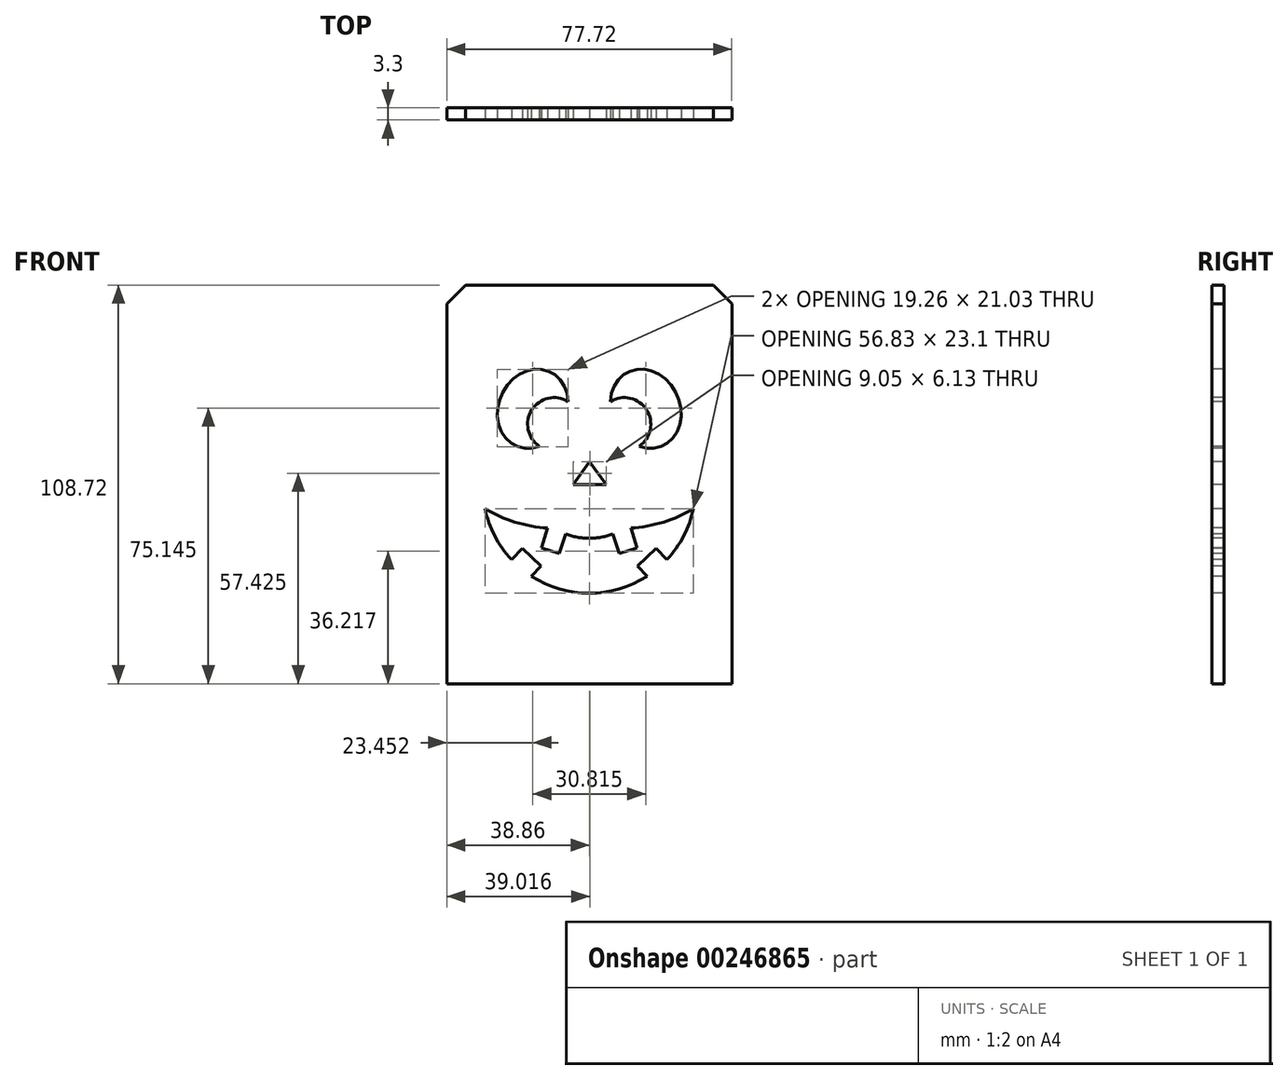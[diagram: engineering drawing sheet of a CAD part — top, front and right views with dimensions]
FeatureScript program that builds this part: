
annotation { "Feature Type Name" : "Feature", "Feature Type Description" : "" }
export const myFeature = defineFeature(function(context is Context, id is Id, definition is map)
    precondition{}
    {
        {
            var Q0;
            Q0=qCreatedBy(makeId("Front.planeOp"),FACE);
            var sketch = newSketch(context, id + "F0", { "sketchPlane" : qUnion([Q0])});
            skLineSegment(sketch, "E0.bottom", {"start": v(38.86, 54.36) * mm, "end": v(-38.86, 54.36) * mm});
            skLineSegment(sketch, "E0.top", {"start": v(38.86, -54.36) * mm, "end": v(-38.86, -54.36) * mm});
            skLineSegment(sketch, "E0.left", {"start": v(38.86, 54.36) * mm, "end": v(38.86, -54.36) * mm});
            skLineSegment(sketch, "E0.right", {"start": v(-38.86, 54.36) * mm, "end": v(-38.86, -54.36) * mm});
            skPoint(sketch, "E0.middle", {"position": v(0, 0) * mm});
            skSolve(sketch);
        }
        {
            var Q0;
            Q0=qSketchRegion(id+"F0",true);
            extrude(context, id + "F1", {"entities" : qUnion([Q0]), "depth" : 3.3 * mm});
        }
        {
            var Q0;
            Q0=makeQuery(id+"F1.opExtrude","CAP_FACE",FACE,{"disambiguationData":[OSD([sQuery(id+"F0.wireOp",EDGE,"E0.bottom"),sQuery(id+"F0.wireOp",EDGE,"E0.top"),sQuery(id+"F0.wireOp",EDGE,"E0.left"),sQuery(id+"F0.wireOp",EDGE,"E0.right")])],"isStart":false});
            var sketch = newSketch(context, id + "F2", { "sketchPlane" : qUnion([Q0])});
            skLineSegment(sketch, "E1", {"start": v(0, 57.24) * mm, "end": v(0, -57.24) * mm, "construction": true});
            skLineSegment(sketch, "E2", {"start": v(-50.8, 0) * mm, "end": v(50.8, 0) * mm, "construction": true});
            skArc(sketch, "E3", {"start": v(35.44, -3.57) * mm, "mid": v(31.46, -11.87) * mm, "end": v(32.26, -21.03) * mm});
            skLineSegment(sketch, "E4", {"start": v(15.88, -44.54) * mm, "end": v(0, -44.54) * mm, "construction": true});
            skArc(sketch, "E5", {"start": v(15.88, -44.54) * mm, "mid": v(30.2, -37.06) * mm, "end": v(32.26, -21.03) * mm});
            skArc(sketch, "E6", {"start": v(15.88, -44.54) * mm, "mid": v(7.78, -45.34) * mm, "end": v(0, -47.71) * mm});
            skArc(sketch, "E7.MirrorCS", {"start": v(-15.87, -44.54) * mm, "mid": v(-7.78, -45.34) * mm, "end": v(0, -47.71) * mm});
            skArc(sketch, "E8.MirrorCS", {"start": v(-15.87, -44.54) * mm, "mid": v(-30.2, -37.06) * mm, "end": v(-32.26, -21.03) * mm});
            skArc(sketch, "E9.MirrorCS", {"start": v(-35.44, -3.57) * mm, "mid": v(-31.46, -11.87) * mm, "end": v(-32.26, -21.03) * mm});
            skArc(sketch, "E10.MirrorCS", {"start": v(-35.44, 3.57) * mm, "mid": v(-31.46, 11.87) * mm, "end": v(-32.26, 21.03) * mm});
            skArc(sketch, "E11.MirrorCS", {"start": v(-15.88, 44.54) * mm, "mid": v(-30.2, 37.06) * mm, "end": v(-32.26, 21.03) * mm});
            skArc(sketch, "E12.MirrorCS", {"start": v(-15.88, 44.54) * mm, "mid": v(-7.78, 45.34) * mm, "end": v(0, 47.71) * mm});
            skArc(sketch, "E13.MirrorCS", {"start": v(15.87, 44.54) * mm, "mid": v(7.78, 45.34) * mm, "end": v(0, 47.71) * mm});
            skArc(sketch, "E14.MirrorCS", {"start": v(15.87, 44.54) * mm, "mid": v(30.2, 37.06) * mm, "end": v(32.26, 21.03) * mm});
            skArc(sketch, "E15.MirrorCS", {"start": v(35.44, 3.57) * mm, "mid": v(31.46, 11.87) * mm, "end": v(32.26, 21.03) * mm});
            skArc(sketch, "E16", {"start": v(35.44, 3.57) * mm, "mid": v(34.41, 0) * mm, "end": v(35.44, -3.57) * mm});
            skPoint(sketch, "E17.orphan", {"position": v(39.69, 0) * mm});
            skArc(sketch, "E18.MirrorCS", {"start": v(-35.44, 3.57) * mm, "mid": v(-34.41, 0) * mm, "end": v(-35.44, -3.57) * mm});
            skPoint(sketch, "E19.orphan", {"position": v(-39.69, 0) * mm});
            skSolve(sketch);
        }
        {
            var Q0;
            Q0=makeQuery(id+"F2.imprint","IMPRINT",FACE,{"disambiguationData":[TD([[makeQuery(id+"F2.imprint","IMPRINT",EDGE,{"derivedFrom":sQuery(id+"F2.wireOp",EDGE,"E3")}),1.0]])]});
            var sketch = newSketch(context, id + "F3", { "sketchPlane" : qUnion([Q0])});
            skFitSpline(sketch, "E20", {"points": [v(-34.74, -25) * mm, v(-17.68, -23.14) * mm, v(0, -25.84) * mm, v(18.3, -28) * mm, v(33.6, -24.4) * mm], "startDerivative": vector(68.08, 28.42) * mm, "endDerivative": vector(41.75, 55.86) * mm});
            skArc(sketch, "E21.0", {"start": v(15.88, -44.54) * mm, "mid": v(28.97, -38.63) * mm, "end": v(33.2, -24.9) * mm});
            skArc(sketch, "E22.0", {"start": v(-15.87, -44.54) * mm, "mid": v(-29.14, -38.43) * mm, "end": v(-33.13, -24.38) * mm});
            skArc(sketch, "E23.0", {"start": v(15.88, -44.54) * mm, "mid": v(7.78, -45.34) * mm, "end": v(0, -47.71) * mm});
            skArc(sketch, "E23.1", {"start": v(-15.87, -44.54) * mm, "mid": v(-7.78, -45.34) * mm, "end": v(0, -47.71) * mm});
            skPoint(sketch, "E24.orphan", {"position": v(-32.26, -21.03) * mm});
            skLineSegment(sketch, "E25.bottom", {"start": v(23.58, -32.65) * mm, "end": v(5.44, -32.65) * mm, "construction": true});
            skLineSegment(sketch, "E25.top", {"start": v(23.58, -12.55) * mm, "end": v(5.44, -12.55) * mm, "construction": true});
            skLineSegment(sketch, "E25.left", {"start": v(23.58, -32.65) * mm, "end": v(23.58, -12.55) * mm, "construction": true});
            skLineSegment(sketch, "E25.right", {"start": v(5.44, -32.65) * mm, "end": v(5.44, -12.55) * mm, "construction": true});
            skArc(sketch, "E26", {"start": v(6.5, -26.77) * mm, "mid": v(6.6, -19.6) * mm, "end": v(5.44, -12.55) * mm});
            skArc(sketch, "E27", {"start": v(23.58, -12.55) * mm, "mid": v(22.47, -20.37) * mm, "end": v(22.78, -28.26) * mm});
            skLineSegment(sketch, "E28", {"start": v(0.57, -13.45) * mm, "end": v(5.44, -12.55) * mm});
            skLineSegment(sketch, "E29", {"start": v(28.46, 0) * mm, "end": v(0.57, 0) * mm, "construction": true});
            skArc(sketch, "E30", {"start": v(-2.4, -8.48) * mm, "mid": v(-2.65, -12) * mm, "end": v(0.57, -13.45) * mm});
            skArc(sketch, "E31", {"start": v(0, -10.42) * mm, "mid": v(-0.23, -8.24) * mm, "end": v(-2.4, -8.48) * mm});
            skArc(sketch, "E32", {"start": v(0, -10.42) * mm, "mid": v(-0.04, -11.92) * mm, "end": v(1.4, -12.35) * mm});
            skArc(sketch, "E33", {"start": v(1.4, -12.35) * mm, "mid": v(5.55, -5.86) * mm, "end": v(0.57, 0) * mm});
            skLineSegment(sketch, "E34", {"start": v(14.51, 0) * mm, "end": v(14.51, -12.55) * mm, "construction": true});
            skArc(sketch, "E35.MirrorCS", {"start": v(27.61, -12.35) * mm, "mid": v(23.47, -5.86) * mm, "end": v(28.46, 0) * mm});
            skLineSegment(sketch, "E36.MirrorCS", {"start": v(28.46, -13.45) * mm, "end": v(23.58, -12.55) * mm});
            skArc(sketch, "E37.MirrorCS", {"start": v(31.42, -8.48) * mm, "mid": v(31.67, -12) * mm, "end": v(28.46, -13.45) * mm});
            skArc(sketch, "E38.MirrorCS", {"start": v(29.02, -10.42) * mm, "mid": v(29.25, -8.24) * mm, "end": v(31.42, -8.48) * mm});
            skArc(sketch, "E39.MirrorCS", {"start": v(29.02, -10.42) * mm, "mid": v(29.06, -11.92) * mm, "end": v(27.61, -12.35) * mm});
            skArc(sketch, "E40", {"start": v(0.57, 0) * mm, "mid": v(5.65, -0.6) * mm, "end": v(10.76, -0.93) * mm});
            skLineSegment(sketch, "E41", {"start": v(10.76, -0.93) * mm, "end": v(8.47, 9.06) * mm});
            skLineSegment(sketch, "E42", {"start": v(8.47, 9.06) * mm, "end": v(6.8, 8.68) * mm});
            skArc(sketch, "E43", {"start": v(7.7, 9.94) * mm, "mid": v(5.6, 10.49) * mm, "end": v(6.8, 8.68) * mm});
            skLineSegment(sketch, "E44", {"start": v(14.51, 0) * mm, "end": v(14.77, 8.31) * mm, "construction": true});
            skLineSegment(sketch, "E45.MirrorCS", {"start": v(18.26, -0.93) * mm, "end": v(21.1, 8.66) * mm});
            skLineSegment(sketch, "E46.MirrorCS", {"start": v(21.1, 8.66) * mm, "end": v(22.75, 8.18) * mm});
            skArc(sketch, "E47.MirrorCS", {"start": v(21.93, 9.5) * mm, "mid": v(24.07, 9.9) * mm, "end": v(22.75, 8.18) * mm});
            skArc(sketch, "E48", {"start": v(7.7, 9.94) * mm, "mid": v(12.62, 15.22) * mm, "end": v(14.1, 22.28) * mm});
            skArc(sketch, "E49", {"start": v(15.59, 22.28) * mm, "mid": v(17.1, 15.06) * mm, "end": v(21.93, 9.5) * mm});
            skLineSegment(sketch, "E50", {"start": v(14.1, 22.28) * mm, "end": v(12.75, 29.94) * mm});
            skLineSegment(sketch, "E51", {"start": v(12.75, 29.94) * mm, "end": v(10.25, 29.5) * mm});
            skLineSegment(sketch, "E52", {"start": v(10.25, 29.5) * mm, "end": v(10.04, 30.72) * mm});
            skLineSegment(sketch, "E53", {"start": v(10.04, 30.72) * mm, "end": v(12.66, 31.3) * mm});
            skLineSegment(sketch, "E54", {"start": v(12.66, 31.3) * mm, "end": v(12.12, 34.79) * mm});
            skLineSegment(sketch, "E55", {"start": v(12.12, 34.79) * mm, "end": v(14.24, 35.11) * mm});
            skLineSegment(sketch, "E56", {"start": v(14.24, 35.11) * mm, "end": v(14.8, 31.45) * mm});
            skLineSegment(sketch, "E57", {"start": v(14.8, 31.45) * mm, "end": v(17.72, 31.9) * mm});
            skLineSegment(sketch, "E58", {"start": v(17.72, 31.9) * mm, "end": v(17.99, 30.17) * mm});
            skLineSegment(sketch, "E59", {"start": v(17.99, 30.17) * mm, "end": v(14.89, 29.68) * mm});
            skLineSegment(sketch, "E60", {"start": v(14.89, 29.68) * mm, "end": v(15.59, 22.28) * mm});
            skArc(sketch, "E61.trimOffspring", {"start": v(18.26, -0.93) * mm, "mid": v(23.37, -0.6) * mm, "end": v(28.46, 0) * mm});
            skPoint(sketch, "E62.orphan", {"position": v(18.2, -1.17) * mm});
            skLineSegment(sketch, "E63", {"start": v(8.48, -4.98) * mm, "end": v(9.12, -7.41) * mm});
            skLineSegment(sketch, "E64", {"start": v(9.77, -9.85) * mm, "end": v(10.94, -9.54) * mm});
            skLineSegment(sketch, "E65", {"start": v(12.72, -9.06) * mm, "end": v(12.26, -7.34) * mm});
            skLineSegment(sketch, "E66", {"start": v(11.56, -4.7) * mm, "end": v(10.33, -4.82) * mm});
            skLineSegment(sketch, "E67", {"start": v(9.75, -4.87) * mm, "end": v(10.34, -7.13) * mm});
            skLineSegment(sketch, "E68", {"start": v(10.34, -7.13) * mm, "end": v(9.12, -7.41) * mm});
            skLineSegment(sketch, "E69", {"start": v(10.33, -4.82) * mm, "end": v(10.9, -7.06) * mm});
            skLineSegment(sketch, "E70", {"start": v(10.9, -7.06) * mm, "end": v(12.14, -6.89) * mm});
            skLineSegment(sketch, "E71", {"start": v(9.29, -8.05) * mm, "end": v(10.46, -7.73) * mm});
            skLineSegment(sketch, "E72", {"start": v(10.46, -7.73) * mm, "end": v(10.94, -9.54) * mm});
            skLineSegment(sketch, "E73", {"start": v(11.57, -9.37) * mm, "end": v(11.12, -7.64) * mm});
            skLineSegment(sketch, "E74", {"start": v(11.12, -7.64) * mm, "end": v(12.26, -7.34) * mm});
            skLineSegment(sketch, "E75.trimOffspring", {"start": v(12.14, -6.89) * mm, "end": v(11.56, -4.7) * mm});
            skLineSegment(sketch, "E76.trimOffspring", {"start": v(9.75, -4.87) * mm, "end": v(8.48, -4.98) * mm});
            skLineSegment(sketch, "E77.trimOffspring", {"start": v(9.29, -8.05) * mm, "end": v(9.77, -9.85) * mm});
            skLineSegment(sketch, "E78.trimOffspring", {"start": v(11.57, -9.37) * mm, "end": v(12.72, -9.06) * mm});
            skLineSegment(sketch, "E79.MirrorCS", {"start": v(17.46, -4.7) * mm, "end": v(18.69, -4.82) * mm});
            skLineSegment(sketch, "E80.MirrorCS", {"start": v(19.27, -4.87) * mm, "end": v(18.68, -7.13) * mm});
            skLineSegment(sketch, "E81.MirrorCS", {"start": v(17.45, -9.37) * mm, "end": v(17.9, -7.64) * mm});
            skLineSegment(sketch, "E82.MirrorCS", {"start": v(18.68, -7.13) * mm, "end": v(19.9, -7.41) * mm});
            skLineSegment(sketch, "E83.MirrorCS", {"start": v(17.9, -7.64) * mm, "end": v(16.76, -7.34) * mm});
            skLineSegment(sketch, "E84.MirrorCS", {"start": v(18.69, -4.82) * mm, "end": v(18.12, -7.06) * mm});
            skLineSegment(sketch, "E85.MirrorCS", {"start": v(16.88, -6.89) * mm, "end": v(17.46, -4.7) * mm});
            skLineSegment(sketch, "E86.MirrorCS", {"start": v(18.12, -7.06) * mm, "end": v(16.88, -6.89) * mm});
            skLineSegment(sketch, "E87.MirrorCS", {"start": v(19.27, -4.87) * mm, "end": v(20.54, -4.98) * mm});
            skLineSegment(sketch, "E88.MirrorCS", {"start": v(20.54, -4.98) * mm, "end": v(19.9, -7.41) * mm});
            skLineSegment(sketch, "E89.MirrorCS", {"start": v(19.73, -8.05) * mm, "end": v(18.56, -7.73) * mm});
            skLineSegment(sketch, "E90.MirrorCS", {"start": v(19.73, -8.05) * mm, "end": v(19.25, -9.85) * mm});
            skLineSegment(sketch, "E91.MirrorCS", {"start": v(19.25, -9.85) * mm, "end": v(18.08, -9.54) * mm});
            skLineSegment(sketch, "E92.MirrorCS", {"start": v(18.56, -7.73) * mm, "end": v(18.08, -9.54) * mm});
            skLineSegment(sketch, "E93.MirrorCS", {"start": v(17.45, -9.37) * mm, "end": v(16.3, -9.06) * mm});
            skLineSegment(sketch, "E94.MirrorCS", {"start": v(16.3, -9.06) * mm, "end": v(16.76, -7.34) * mm});
            skArc(sketch, "E95", {"start": v(14.28, 11.97) * mm, "mid": v(12.23, 10.98) * mm, "end": v(11.15, 8.98) * mm});
            skLineSegment(sketch, "E96", {"start": v(14.28, 11.97) * mm, "end": v(14.28, 8.98) * mm});
            skLineSegment(sketch, "E97", {"start": v(15.17, 4.65) * mm, "end": v(15.17, 7.88) * mm});
            skLineSegment(sketch, "E98", {"start": v(18.4, 8.98) * mm, "end": v(15.17, 8.98) * mm});
            skLineSegment(sketch, "E99", {"start": v(11.1, 7.88) * mm, "end": v(14.28, 7.88) * mm});
            skLineSegment(sketch, "E100.trimOffspring", {"start": v(15.17, 8.98) * mm, "end": v(15.17, 11.98) * mm});
            skLineSegment(sketch, "E101.trimOffspring", {"start": v(15.17, 7.88) * mm, "end": v(18.43, 7.88) * mm});
            skLineSegment(sketch, "E102.trimOffspring", {"start": v(14.28, 7.88) * mm, "end": v(14.28, 4.66) * mm});
            skLineSegment(sketch, "E103.trimOffspring", {"start": v(14.28, 8.98) * mm, "end": v(11.15, 8.98) * mm});
            skArc(sketch, "E104.trimOffspring", {"start": v(11.1, 7.88) * mm, "mid": v(12.14, 5.73) * mm, "end": v(14.28, 4.66) * mm});
            skArc(sketch, "E105.trimOffspring", {"start": v(18.4, 8.98) * mm, "mid": v(17.28, 11.01) * mm, "end": v(15.17, 11.98) * mm});
            skArc(sketch, "E106.trimOffspring", {"start": v(15.17, 4.65) * mm, "mid": v(17.37, 5.7) * mm, "end": v(18.43, 7.88) * mm});
            skLineSegment(sketch, "E107.left", {"start": v(12.04, -27.4) * mm, "end": v(12.04, -21.48) * mm});
            skLineSegment(sketch, "E107.right", {"start": v(16, -27.8) * mm, "end": v(16, -21.48) * mm});
            skArc(sketch, "E108", {"start": v(16, -21.48) * mm, "mid": v(14.02, -19.5) * mm, "end": v(12.04, -21.48) * mm});
            skLineSegment(sketch, "E109", {"start": v(12.04, -27.4) * mm, "end": v(16, -27.8) * mm});
            skArc(sketch, "E110.0", {"start": v(-35.44, -3.57) * mm, "mid": v(-31.46, -11.87) * mm, "end": v(-32.26, -21.03) * mm, "construction": true});
            skArc(sketch, "E110.1", {"start": v(15.87, 44.54) * mm, "mid": v(7.78, 45.34) * mm, "end": v(0, 47.71) * mm});
            skArc(sketch, "E110.2", {"start": v(-15.88, 44.54) * mm, "mid": v(-30.2, 37.06) * mm, "end": v(-32.26, 21.03) * mm, "construction": true});
            skArc(sketch, "E110.3", {"start": v(-35.44, 3.57) * mm, "mid": v(-34.41, 0) * mm, "end": v(-35.44, -3.57) * mm, "construction": true});
            skArc(sketch, "E110.4", {"start": v(-35.44, 3.57) * mm, "mid": v(-31.46, 11.87) * mm, "end": v(-32.26, 21.03) * mm});
            skArc(sketch, "E110.5", {"start": v(-15.88, 44.54) * mm, "mid": v(-7.78, 45.34) * mm, "end": v(0, 47.71) * mm});
            skArc(sketch, "E111", {"start": v(-17.1, 9.66) * mm, "mid": v(-3.37, 14.89) * mm, "end": v(1.5, 28.74) * mm});
            skArc(sketch, "E112", {"start": v(-17.1, 9.66) * mm, "mid": v(-26.87, 8.42) * mm, "end": v(-35.44, 3.57) * mm});
            skArc(sketch, "E113", {"start": v(15.87, 44.54) * mm, "mid": v(5.2, 39.82) * mm, "end": v(1.5, 28.74) * mm});
            skArc(sketch, "E114.trimOffspring", {"start": v(-15.88, 44.54) * mm, "mid": v(-30.2, 37.06) * mm, "end": v(-32.26, 21.03) * mm});
            skArc(sketch, "E115", {"start": v(-24.92, -22.89) * mm, "mid": v(-23.55, -16.2) * mm, "end": v(-24.4, -9.44) * mm});
            skFitSpline(sketch, "E116", {"points": [v(-24.4, -9.44) * mm, v(-26.98, -10.38) * mm, v(-27.97, -8.39) * mm, v(-29.93, -8.52) * mm, v(-30.92, -6) * mm, v(-32.1, -5.52) * mm, v(-32.53, -4.18) * mm, v(-32.18, -3.27) * mm, v(-31.84, -4.44) * mm, v(-31.05, -4.83) * mm, v(-31.49, -2) * mm, v(-30.88, -2.14) * mm, v(-30.1, -5.05) * mm, v(-29.45, -3.57) * mm, v(-28.71, -3.66) * mm, v(-29.54, -5.78) * mm, v(-29.23, -7.17) * mm, v(-27.54, -7.04) * mm, v(-26.28, -8.52) * mm, v(-24.4, -7.6) * mm], "startDerivative": vector(-46.53, -30.94) * mm, "endDerivative": vector(36.03, 29.74) * mm});
            skArc(sketch, "E117", {"start": v(-24.4, -7.6) * mm, "mid": v(-24.93, -4.98) * mm, "end": v(-25.9, -2.49) * mm});
            skFitSpline(sketch, "E118", {"points": [v(-25.9, -2.49) * mm, v(-27.5, -1.49) * mm, v(-28.76, -1.49) * mm, v(-29.23, 0) * mm, v(-31.14, 0) * mm, v(-30.8, 3.42) * mm, v(-29.97, 3.55) * mm, v(-30.27, 1.77) * mm, v(-29.54, 1.72) * mm, v(-28.8, 4.59) * mm, v(-27.67, 4.37) * mm, v(-28.28, 1.98) * mm, v(-27.84, 0) * mm, v(-27.2, 2.46) * mm, v(-25.9, 2.37) * mm, v(-25.9, 0) * mm, v(-24.11, -2.49) * mm, v(-22.72, -5.26) * mm, v(-21.68, -4.18) * mm, v(-23.16, 1.33) * mm, v(-20.82, 1.46) * mm, v(-20.82, 3.02) * mm], "startDerivative": vector(-33.14, 31.82) * mm, "endDerivative": vector(-15.18, 49.9) * mm});
            skFitSpline(sketch, "E119", {"points": [v(-20.82, 3.02) * mm, v(-19.2, 3.92) * mm, v(-20.04, 5.84) * mm, v(-20.82, 8.3) * mm, v(-20.04, 8.38) * mm, v(-19.62, 6.46) * mm, v(-18.62, 5.34) * mm, v(-18.96, 7.3) * mm, v(-18.2, 7.55) * mm, v(-18.12, 4.13) * mm, v(-19.33, 2.25) * mm, v(-19.46, 0.87) * mm, v(-20.82, 0) * mm, v(-20.04, -3.35) * mm, v(-16.32, 0) * mm, v(-17.1, 1.46) * mm, v(-15.74, 3.02) * mm, v(-15.45, 5.84) * mm, v(-14.49, 5.55) * mm, v(-14.82, 3.02) * mm, v(-14.53, 1.46) * mm, v(-13.36, 4) * mm, v(-12.02, 3.02) * mm, v(-14.2, 0) * mm, v(-17.1, -4.06) * mm, v(-17.1, -7.4) * mm, v(-14.36, -5.44) * mm, v(-14.57, -4.1) * mm, v(-12.78, -3.22) * mm, v(-12.53, -1.68) * mm, v(-10.44, -0.8) * mm, v(-10.27, 1.46) * mm, v(-9.35, 0) * mm, v(-8.6, 3.02) * mm, v(-8.1, 0) * mm, v(-9.44, -1.26) * mm, v(-11.31, -3.26) * mm, v(-13.15, -4.6) * mm, v(-13.36, -6.6) * mm, v(-15.78, -8.94) * mm], "startDerivative": vector(94.65, 30.69) * mm, "endDerivative": vector(-102.82, -69.25) * mm});
            skArc(sketch, "E120", {"start": v(-15.78, -8.94) * mm, "mid": v(-16.8, -16.14) * mm, "end": v(-15.78, -23.34) * mm});
            skFitSpline(sketch, "E121", {"points": [v(-22.4, -11.55) * mm, v(-21.43, -13.07) * mm, v(-21.4, -14.11) * mm, v(-20.72, -14.36) * mm, v(-20.54, -13.59) * mm, v(-20.94, -12.02) * mm, v(-21.71, -11.06) * mm, v(-22.67, -10.07) * mm, v(-22.4, -11.55) * mm]});
            skFitSpline(sketch, "E122", {"points": [v(-18.38, -10.1) * mm, v(-19.09, -11.5) * mm, v(-19.21, -12.7) * mm, v(-19.15, -14.02) * mm, v(-18.84, -14.6) * mm, v(-18.38, -14.05) * mm, v(-18.26, -13.1) * mm, v(-18.56, -12.32) * mm, v(-18.29, -11.28) * mm, v(-17.6, -10.38) * mm, v(-18.38, -10.1) * mm]});
            skFitSpline(sketch, "E123", {"points": [v(-20.3, -15.78) * mm, v(-20.35, -17.1) * mm, v(-20.9, -18.47) * mm, v(-21.8, -19.67) * mm, v(-21.9, -21.46) * mm, v(-20.45, -21.43) * mm, v(-19.64, -20.38) * mm, v(-19.43, -18.84) * mm, v(-19.7, -17.85) * mm, v(-19.7, -16.37) * mm, v(-19.43, -15.38) * mm, v(-20.3, -15.78) * mm]});
            skCircle(sketch, "E124", {"center": v(-15.88, 27.08) * mm, "radius": 13.34 * mm});
            skSolve(sketch);
        }
        {
            var Q0;
            Q0=qSketchRegion(id+"F3",true);
            extrude(context, id + "F4", {"entities" : qUnion([Q0]), "operationType" : NewBodyOperationType.ADD, "oppositeDirection" : true, "depth" : 3.3 * mm});
        }
        {
            var Q0;
            Q0=makeQuery(id+"F1.opExtrude","SWEPT_EDGE",EDGE,{"disambiguationData":[OSD([sQuery(id+"F0.wireOp",EDGE,"E0.bottom"),sQuery(id+"F0.wireOp",EDGE,"E0.right")])]});
            var Q1;
            Q1=makeQuery(id+"F1.opExtrude","SWEPT_EDGE",EDGE,{"disambiguationData":[OSD([sQuery(id+"F0.wireOp",EDGE,"E0.bottom"),sQuery(id+"F0.wireOp",EDGE,"E0.left")])]});
            chamfer(context, id + "F5", {"entities" : qUnion([Q0, Q1]), "width" : 5.08 * mm, "tangentPropagation" : true});
        }
        {
            var Q0;
            Q0=makeQuery(id+"F2.imprint","IMPRINT",FACE,{"disambiguationData":[TD([[makeQuery(id+"F2.imprint","IMPRINT",EDGE,{"derivedFrom":sQuery(id+"F2.wireOp",EDGE,"E3")}),-1.0]])]});
            var sketch = newSketch(context, id + "F6", { "sketchPlane" : qUnion([Q0])});
            skEllipticalArc(sketch, "E125", {});
            skArc(sketch, "E126", {"start": v(13.61, 10.39) * mm, "mid": v(15.64, 20.31) * mm, "end": v(5.78, 22.6) * mm});
            skLineSegment(sketch, "E127", {"start": v(0, 6.13) * mm, "end": v(-4.37, 0) * mm});
            skLineSegment(sketch, "E128", {"start": v(-4.37, 0) * mm, "end": v(4.68, 0) * mm});
            skLineSegment(sketch, "E129", {"start": v(4.68, 0) * mm, "end": v(0, 6.13) * mm});
            skArc(sketch, "E130", {"start": v(0, -29.7) * mm, "mid": v(8.21, -28.5) * mm, "end": v(15.75, -25.05) * mm});
            skLineSegment(sketch, "E131", {"start": v(0, -29.7) * mm, "end": v(-13.21, -29.7) * mm, "construction": true});
            skLineSegment(sketch, "E132", {"start": v(15.75, -25.05) * mm, "end": v(13.12, -22.27) * mm});
            skLineSegment(sketch, "E133", {"start": v(13.12, -22.27) * mm, "end": v(18.25, -17.41) * mm});
            skLineSegment(sketch, "E134", {"start": v(18.25, -17.41) * mm, "end": v(21.18, -20.51) * mm});
            skArc(sketch, "E135", {"start": v(21.18, -20.51) * mm, "mid": v(25.76, -14.05) * mm, "end": v(28.42, -6.6) * mm});
            skArc(sketch, "E136", {"start": v(11.32, -11.88) * mm, "mid": v(20.2, -10.3) * mm, "end": v(28.42, -6.6) * mm});
            skLineSegment(sketch, "E137", {"start": v(11.32, -11.88) * mm, "end": v(13.01, -17.26) * mm});
            skLineSegment(sketch, "E138", {"start": v(13.01, -17.26) * mm, "end": v(8.13, -18.8) * mm});
            skLineSegment(sketch, "E139", {"start": v(8.13, -18.8) * mm, "end": v(6.47, -13.5) * mm});
            skArc(sketch, "E140", {"start": v(0, -14.68) * mm, "mid": v(3.3, -14.41) * mm, "end": v(6.47, -13.5) * mm});
            skEllipticalArc(sketch, "E141.MirrorCS", {});
            skArc(sketch, "E142.MirrorCS", {"start": v(-13.61, 10.39) * mm, "mid": v(-15.64, 20.31) * mm, "end": v(-5.78, 22.6) * mm});
            skArc(sketch, "E143.MirrorCS", {"start": v(-11.32, -11.88) * mm, "mid": v(-20.2, -10.3) * mm, "end": v(-28.42, -6.6) * mm});
            skArc(sketch, "E144.MirrorCS", {"start": v(-21.18, -20.51) * mm, "mid": v(-25.76, -14.05) * mm, "end": v(-28.42, -6.6) * mm});
            skLineSegment(sketch, "E145.MirrorCS", {"start": v(-11.32, -11.88) * mm, "end": v(-13.01, -17.26) * mm});
            skLineSegment(sketch, "E146.MirrorCS", {"start": v(-13.01, -17.26) * mm, "end": v(-8.13, -18.8) * mm});
            skLineSegment(sketch, "E147.MirrorCS", {"start": v(-8.13, -18.8) * mm, "end": v(-6.47, -13.5) * mm});
            skArc(sketch, "E148.MirrorCS", {"start": v(0, -14.68) * mm, "mid": v(-3.3, -14.41) * mm, "end": v(-6.47, -13.5) * mm});
            skArc(sketch, "E149.MirrorCS", {"start": v(0, -29.7) * mm, "mid": v(-8.21, -28.5) * mm, "end": v(-15.75, -25.05) * mm});
            skLineSegment(sketch, "E150.MirrorCS", {"start": v(-15.75, -25.05) * mm, "end": v(-13.12, -22.27) * mm});
            skLineSegment(sketch, "E151.MirrorCS", {"start": v(-13.12, -22.27) * mm, "end": v(-18.25, -17.41) * mm});
            skLineSegment(sketch, "E152.MirrorCS", {"start": v(-18.25, -17.41) * mm, "end": v(-21.18, -20.51) * mm});
            const initialGuessF6  = {"E125": [0.015410825610160828, 0.020649045705795288, 0.41665497605365237, -0.9090647011790363, 0.011105577364097861, 0.009311049041859877, 5.595469094661962, 4.163275475639217], "E141.MirrorCS": [-0.015410825610928406, 0.02064904570522219, -0.41665497601984613, -0.9090647011945308, 0.011105577364097861, 0.009311049041859877, 2.119909831540369, 0.6877162125176239]};
            skSetInitialGuess(sketch, initialGuessF6);
            skSolve(sketch);
        }
        {
            var Q0;
            Q0=qSketchRegion(id+"F6",true);
            extrude(context, id + "F7", {"entities" : qUnion([Q0]), "operationType" : NewBodyOperationType.REMOVE, "endBound" : BoundingType.THROUGH_ALL, "oppositeDirection" : true, "depth" : 25.4 * mm});
        }
    });
